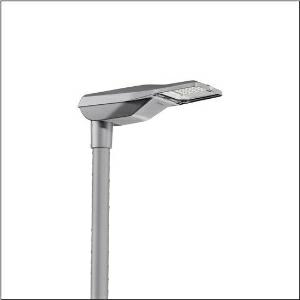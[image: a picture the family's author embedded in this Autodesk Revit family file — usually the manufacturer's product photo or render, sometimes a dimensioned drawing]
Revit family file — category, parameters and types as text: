
# Revit family: streetlight_sl_21_iq_micro___stw1_0a_5xe1e61g08cb_7f5e
name_source: partatom
category: Lighting Fixtures
units: mm (PartAtom-declared; Revit-internal decimal feet)

## family parameters
Cut with Voids When Loaded = No
Host = Face
Light Source = No
Part Type = Normal
Room Calculation Point = No
Round Connector Dimension = Use Diameter
Shared = No

## types (1)
- --- (1 x LED, 2570 lm, 19.4 W, 2700K)
    Apparent Load = 19 VA
    CIE Flux Codes = 38 75 98 100 100
    Color Rendering = 70
    Color Temperature = 2700K
    Default Elevation = 1800 mm
    Description = Streetlight SL 21 iQ micro, mast luminaire, primary light control with lens, of PMMA, primary optical cover: cover, of toughened safety glass, transparent, light distribution: STW1.0a, light emission: direct distribution, primary light characteristic: asymmetric, installation type: post-top, side-entry, LED, High Power LED, rated luminous flux: 2.570lm, luminous efficacy: 133lm/W, light colour: 727, colour temperature: 2700K, control gear: iQ Street-Remote, control: Street-Remote, Auto-Match, Temp-Guard, Lumen-Switch, Night-Set, Smart-Wire, Light-Fading, Desk-Remote (wireless, voltage-free reading and setting of iQ features in the workshop via application-optimized NFC function/RFID function), optimised constant luminous flux control (CLO 2.0), pre-setting: linear dimming characteristic, mains connection: 220..240V, AC, 50/60Hz, start of lifetime: 19W, end of service life: 20W, reduction: 10W, luminaire housing, of diecast aluminium, powder-coated, Siteco® metallic grey (DB 702S), corrosivity category C5 mid according to DIN EN ISO 12944, please order mast flange separately, inclination adjustable: 0°, 5°, 10°, 15°, sealing non-destructively replaceable, multi-level sealing system, length: 528mm, width: 235mm, height: 110mm, mast flange for spigot size: 42mm (side-entry): 5XC10008XM4, 60/48mm (side-entry/post-top): 5XC10108XM2, 76/60mm (side-entry/post-top): 5XC10108XM1, protection rating (complete): IP66, insulation class (complete): insulation class II (safety insulation), certification: CE, ENEC, ENEC+, VDE, impact resistance: IK10, permissible operating ambient temperature for outdoor applications: -40..+50°C, standard-compliant lighting for roads and squares, packaging unit: 1 piece

Light Distribution: STW1.0a
    Height = 110 mm
    Lamp = 1 x LED
    Lamp Light Flux = 2570 lm
    Lamp Power = 19.4 W
    Lamp count = 1
    Length = 528 mm
    Luminous efficacy = 132 lm/W
    Manufacturer = Siteco
    ModVariant = No
    Model = 5XE1E61G08CB
    Number of Poles = 1
    OnlyDefault = Yes
    Power Factor = 1
    Product Name = Streetlight SL 21 iQ micro | STW1.0a
    Product group = mast luminaire | pylon top
    ProductGroupID = 6100
    Protection Class = Protection class II
    Protection Degree = IP 66
    RLX_Detail_Level = 1
    RLX_Emergency_Light_Flux = 0 lm
    RLX_Emergency_Type = 0
    RLX_Emergency_Type_DB = No
    RlxData = <blob elided: 98845 chars, md5=5a34d367>
    Socket = socket
    Standby Power = 0 W
    System Light Flux = 2570 lm
    System Power = 19 W
    Type Comments = factory setting: luminous flux: 100 % | dim-lin: 254 | 387 mA
    Type Image = l_1006881.jpg
    URL = http://relux.com
    VarID = @adj_160195
    Voltage = 0 V
    Weight = 0.00 kg
    Width = 235 mm

## geometry (parser evidence)
native form markers: Blend x4, Sweep x10
no freeform markers — native parametric forms only
